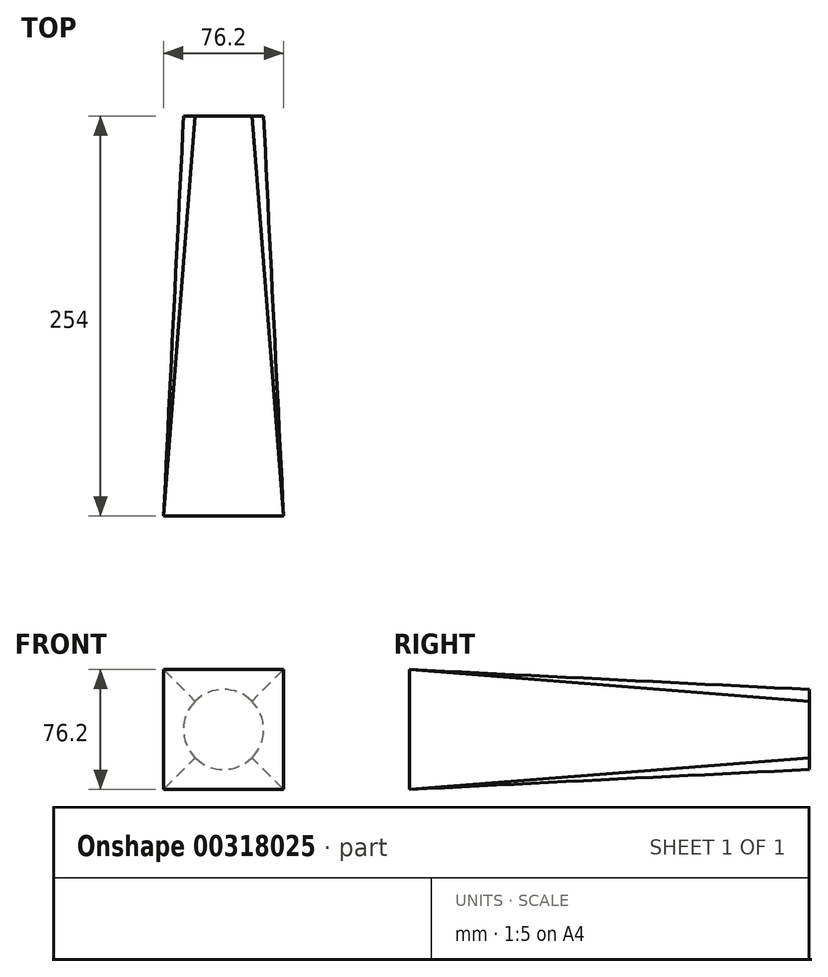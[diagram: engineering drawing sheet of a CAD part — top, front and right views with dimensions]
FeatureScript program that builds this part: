
annotation { "Feature Type Name" : "Feature", "Feature Type Description" : "" }
export const myFeature = defineFeature(function(context is Context, id is Id, definition is map)
    precondition{}
    {
        {
            var Q0;
            Q0=qCreatedBy(makeId("Front.planeOp"),FACE);
            var sketch = newSketch(context, id + "F0", { "sketchPlane" : qUnion([Q0])});
            skLineSegment(sketch, "E0.bottom", {"start": v(-38.1, 38.1) * mm, "end": v(38.1, 38.1) * mm});
            skLineSegment(sketch, "E0.top", {"start": v(-38.1, -38.1) * mm, "end": v(38.1, -38.1) * mm});
            skLineSegment(sketch, "E0.left", {"start": v(-38.1, 38.1) * mm, "end": v(-38.1, -38.1) * mm});
            skLineSegment(sketch, "E0.right", {"start": v(38.1, 38.1) * mm, "end": v(38.1, -38.1) * mm});
            skPoint(sketch, "E0.middle", {"position": v(0, 0) * mm});
            skSolve(sketch);
        }
        {
            var Q0;
            Q0=qCreatedBy(makeId("Front.planeOp"),FACE);
            cPlane(context, id + "F1", {"entities" : qUnion([Q0]), "cplaneType" : CPlaneType.OFFSET, "offset" : 254 * mm, "oppositeDirection" : true, "width" : 152.4 * mm, "height" : 152.4 * mm});
        }
        {
            var Q0;
            Q0=qCreatedBy(id+"F1.planeOp",FACE);
            var sketch = newSketch(context, id + "F2", { "sketchPlane" : qUnion([Q0])});
            skCircle(sketch, "E1", {"center": v(0, 0) * mm, "radius": 25.4 * mm});
            skSolve(sketch);
        }
        {
            var Q0;
            Q0=makeQuery(id+"F0.imprint","IMPRINT",FACE,{"disambiguationData":[TD([[makeQuery(id+"F0.imprint","IMPRINT",EDGE,{"derivedFrom":sQuery(id+"F0.wireOp",EDGE,"E0.bottom")}),-1.0]])]});
            var Q1;
            Q1=makeQuery(id+"F2.imprint","IMPRINT",FACE,{"disambiguationData":[TD([[makeQuery(id+"F2.imprint","IMPRINT",EDGE,{"derivedFrom":sQuery(id+"F2.wireOp",EDGE,"E1")}),1.0]])]});
            loft(context, id + "F3", {"sheetProfilesArray" : [{ "sheetProfileEntities" : qUnion([Q0]) }, { "sheetProfileEntities" : qUnion([Q1]) }]});
        }
    });
